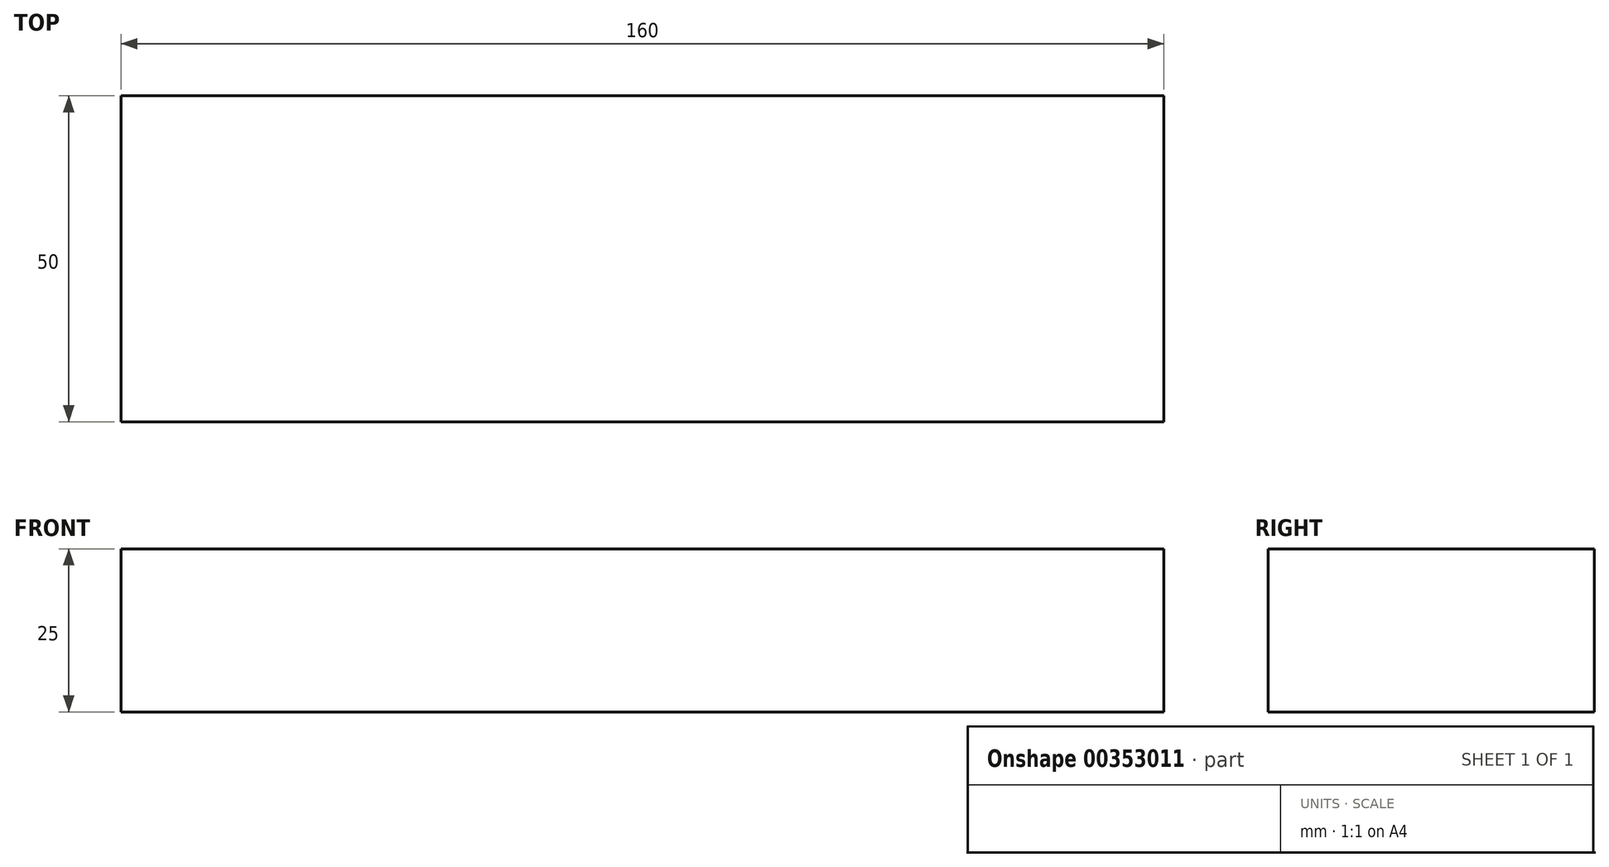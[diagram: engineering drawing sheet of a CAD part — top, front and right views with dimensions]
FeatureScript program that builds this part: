
annotation { "Feature Type Name" : "Feature", "Feature Type Description" : "" }
export const myFeature = defineFeature(function(context is Context, id is Id, definition is map)
    precondition{}
    {
        {
            var Q0;
            Q0=qCreatedBy(makeId("Top.planeOp"),FACE);
            var sketch = newSketch(context, id + "F0", { "sketchPlane" : qUnion([Q0])});
            skLineSegment(sketch, "E0", {"start": v(0, 0) * mm, "end": v(0, 50) * mm});
            skLineSegment(sketch, "E1", {"start": v(0, 50) * mm, "end": v(160, 50) * mm});
            skLineSegment(sketch, "E2", {"start": v(160, 50) * mm, "end": v(160, 0) * mm});
            skLineSegment(sketch, "E3", {"start": v(160, 0) * mm, "end": v(0, 0) * mm});
            skSolve(sketch);
        }
        {
            var Q0;
            Q0 = qSketchRegion(id + "F0", true);
            extrude(context, id + "F1", {"entities" : qUnion([Q0]), "depth" : 25 * mm});
        }
    });
